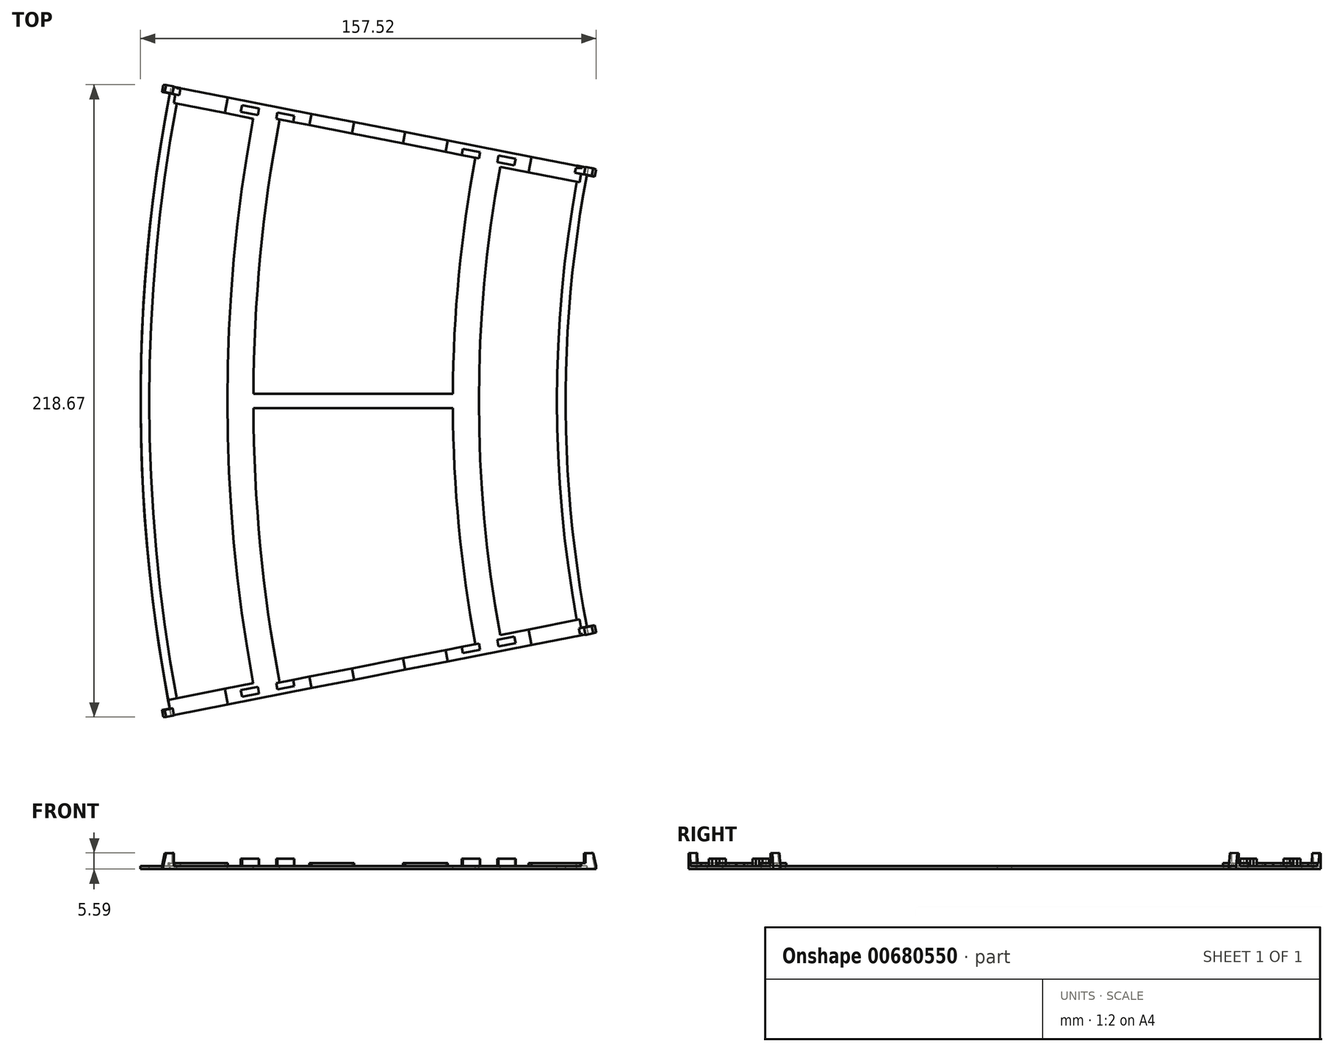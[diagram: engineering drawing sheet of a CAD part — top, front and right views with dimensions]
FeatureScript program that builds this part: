
annotation { "Feature Type Name" : "Feature", "Feature Type Description" : "" }
export const myFeature = defineFeature(function(context is Context, id is Id, definition is map)
    precondition{}
    {
        {
            var Q0;
            Q0=qCreatedBy(makeId("Front.planeOp"),FACE);
            var sketch = newSketch(context, id + "F0", { "sketchPlane" : qUnion([Q0])});
            skLineSegment(sketch, "E0", {"start": v(0, 1.91) * mm, "end": v(570.67, 0) * mm});
            skLineSegment(sketch, "E1", {"start": v(570.67, 0) * mm, "end": v(553.13, -97.53) * mm});
            skLineSegment(sketch, "E2", {"start": v(553.13, -97.53) * mm, "end": v(0, 1.91) * mm});
            skLineSegment(sketch, "E3", {"start": v(0, 1.91) * mm, "end": v(0.03, 10.91) * mm});
            skLineSegment(sketch, "E4", {"start": v(0.03, 10.91) * mm, "end": v(156.03, 10.39) * mm});
            skLineSegment(sketch, "E5", {"start": v(156.03, 10.39) * mm, "end": v(156, 1.39) * mm});
            skLineSegment(sketch, "E6", {"start": v(156, 1.39) * mm, "end": v(155.97, -7.61) * mm});
            skLineSegment(sketch, "E7", {"start": v(155.97, -7.61) * mm, "end": v(-0.03, -7.09) * mm});
            skLineSegment(sketch, "E8", {"start": v(-0.03, -7.09) * mm, "end": v(0, 1.91) * mm});
            skLineSegment(sketch, "E9", {"start": v(4.53, 10.9) * mm, "end": v(4.47, -7.1) * mm});
            skLineSegment(sketch, "E10", {"start": v(151.53, 10.4) * mm, "end": v(151.47, -7.6) * mm});
            skSolve(sketch);
        }
        {
            var Q0;
            {var subQ0=sQuery(id+"F0.wireOp",EDGE,"E9");var subQ1=sQuery(id+"F0.wireOp",EDGE,"E0");var subQ2=makeQuery(id+"F0.imprint","INTERSECT",VERTEX,{"derivedFrom":[subQ1,subQ0]});Q0=makeQuery(id+"F0.imprint","IMPRINT",FACE,{"disambiguationData":[TD([[makeQuery(id+"F0.imprint","IMPRINT",EDGE,{"disambiguationData":[TD([[subQ2,-1.0]])],"derivedFrom":subQ1}),1.0]])]});}
            var Q1;
            {var subQ0=sQuery(id+"F0.wireOp",EDGE,"E9");var subQ1=sQuery(id+"F0.wireOp",EDGE,"E0");var subQ2=makeQuery(id+"F0.imprint","INTERSECT",VERTEX,{"derivedFrom":[subQ1,subQ0]});Q1=makeQuery(id+"F0.imprint","IMPRINT",FACE,{"disambiguationData":[TD([[makeQuery(id+"F0.imprint","IMPRINT",EDGE,{"disambiguationData":[TD([[subQ2,-1.0]])],"derivedFrom":subQ1}),-1.0]])]});}
            var Q2;
            {var subQ0=sQuery(id+"F0.wireOp",EDGE,"E7");var subQ1=sQuery(id+"F0.wireOp",EDGE,"E2");var subQ2=makeQuery(id+"F0.imprint","INTERSECT",VERTEX,{"derivedFrom":[subQ1,subQ0]});Q2=makeQuery(id+"F0.imprint","IMPRINT",FACE,{"disambiguationData":[TD([[makeQuery(id+"F0.imprint","IMPRINT",EDGE,{"disambiguationData":[TD([[subQ2,-1.0]])],"derivedFrom":subQ1}),1.0]])]});}
            var Q3;
            Q3=sQuery(id+"F0.wireOp",EDGE,"E1");
            revolve(context, id + "F1", {"entities" : qUnion([Q0, Q1, Q2]), "axis" : qUnion([Q3]), "revolveType" : RevolveType.SYMMETRIC, "angle" : 22.5 * degree});
        }
        {
            var Q0;
            Q0=qCreatedBy(makeId("Front.planeOp"),FACE);
            var sketch = newSketch(context, id + "F2", { "sketchPlane" : qUnion([Q0])});
            skLineSegment(sketch, "E11.bottom", {"start": v(-4.32, 0) * mm, "end": v(170.27, 0) * mm});
            skLineSegment(sketch, "E11.top", {"start": v(-4.32, -12.77) * mm, "end": v(170.27, -12.77) * mm});
            skLineSegment(sketch, "E11.left", {"start": v(-4.32, 0) * mm, "end": v(-4.32, -12.77) * mm});
            skLineSegment(sketch, "E11.right", {"start": v(170.27, 0) * mm, "end": v(170.27, -12.77) * mm});
            skLineSegment(sketch, "E12.bottom", {"start": v(-4.39, 1) * mm, "end": v(170.27, 1) * mm});
            skLineSegment(sketch, "E12.top", {"start": v(-4.39, 14.98) * mm, "end": v(170.27, 14.98) * mm});
            skLineSegment(sketch, "E12.left", {"start": v(-4.39, 1) * mm, "end": v(-4.39, 14.98) * mm});
            skLineSegment(sketch, "E12.right", {"start": v(170.27, 1) * mm, "end": v(170.27, 14.98) * mm});
            skSolve(sketch);
        }
        {
            var Q0;
            Q0=makeQuery(id+"F2.imprint","IMPRINT",FACE,{"disambiguationData":[TD([[makeQuery(id+"F2.imprint","IMPRINT",EDGE,{"derivedFrom":sQuery(id+"F2.wireOp",EDGE,"E12.bottom")}),1.0]])]});
            var Q1;
            Q1=makeQuery(id+"F2.imprint","IMPRINT",FACE,{"disambiguationData":[TD([[makeQuery(id+"F2.imprint","IMPRINT",EDGE,{"derivedFrom":sQuery(id+"F2.wireOp",EDGE,"E11.bottom")}),-1.0]])]});
            extrude(context, id + "F3", {"entities" : qUnion([Q0, Q1]), "operationType" : NewBodyOperationType.REMOVE, "endBound" : BoundingType.SYMMETRIC, "depth" : 250 * mm, "offsetDistance" : 25 * mm});
        }
        {
            var Q0;
            Q0=makeQuery(id+"F3.boolean.opBoolean","COPY",FACE,{"derivedFrom":makeQuery(id+"F3.opExtrude","SWEPT_FACE",FACE,{"disambiguationData":[OSD([sQuery(id+"F2.wireOp",EDGE,"E12.bottom")])]})});
            var sketch = newSketch(context, id + "F4", { "sketchPlane" : qUnion([Q0])});
            skArc(sketch, "E13", {"start": v(16.97, 102.83) * mm, "mid": v(7.5, 0) * mm, "end": v(16.97, -102.83) * mm});
            skArc(sketch, "E14", {"start": v(43.47, 97.64) * mm, "mid": v(34.5, 0) * mm, "end": v(43.47, -97.64) * mm});
            skArc(sketch, "E15", {"start": v(52.57, 97.39) * mm, "mid": v(45.9, 50.15) * mm, "end": v(43.5, 2.5) * mm});
            skArc(sketch, "E16", {"start": v(120.29, 84.13) * mm, "mid": v(114.57, 43.5) * mm, "end": v(112.5, 2.5) * mm});
            skArc(sketch, "E17", {"start": v(128.85, 80.93) * mm, "mid": v(121.5, 0) * mm, "end": v(128.85, -80.93) * mm});
            skArc(sketch, "E18", {"start": v(155.35, 75.74) * mm, "mid": v(148.5, 0) * mm, "end": v(155.35, -75.74) * mm});
            skLineSegment(sketch, "E19", {"start": v(43.5, 2.5) * mm, "end": v(112.5, 2.5) * mm});
            skLineSegment(sketch, "E20", {"start": v(43.5, -2.5) * mm, "end": v(112.5, -2.5) * mm});
            skArc(sketch, "E21.trimOffspring", {"start": v(43.5, -2.5) * mm, "mid": v(45.9, -50.15) * mm, "end": v(52.57, -97.39) * mm});
            skArc(sketch, "E22.trimOffspring", {"start": v(112.5, -2.5) * mm, "mid": v(114.57, -43.5) * mm, "end": v(120.29, -84.13) * mm});
            skLineSegment(sketch, "E23", {"start": v(16.97, 102.83) * mm, "end": v(43.47, 97.64) * mm});
            skLineSegment(sketch, "E24", {"start": v(52.57, 97.39) * mm, "end": v(120.29, 84.13) * mm});
            skLineSegment(sketch, "E25", {"start": v(128.85, 80.93) * mm, "end": v(155.35, 75.74) * mm});
            skLineSegment(sketch, "E26", {"start": v(16.97, -102.83) * mm, "end": v(43.47, -97.64) * mm});
            skLineSegment(sketch, "E27", {"start": v(52.57, -97.39) * mm, "end": v(120.29, -84.13) * mm});
            skLineSegment(sketch, "E28", {"start": v(128.85, -80.93) * mm, "end": v(155.35, -75.74) * mm});
            skSolve(sketch);
        }
        {
            var Q0;
            Q0=makeQuery(id+"F4.imprint","IMPRINT",FACE,{"disambiguationData":[TD([[makeQuery(id+"F4.imprint","IMPRINT",EDGE,{"derivedFrom":sQuery(id+"F4.wireOp",EDGE,"E13")}),1.0]])]});
            var Q1;
            Q1=makeQuery(id+"F4.imprint","IMPRINT",FACE,{"disambiguationData":[TD([[makeQuery(id+"F4.imprint","IMPRINT",EDGE,{"derivedFrom":sQuery(id+"F4.wireOp",EDGE,"E15")}),1.0]])]});
            var Q2;
            Q2=makeQuery(id+"F4.imprint","IMPRINT",FACE,{"disambiguationData":[TD([[makeQuery(id+"F4.imprint","IMPRINT",EDGE,{"derivedFrom":sQuery(id+"F4.wireOp",EDGE,"E20")}),-1.0]])]});
            var Q3;
            Q3=makeQuery(id+"F4.imprint","IMPRINT",FACE,{"disambiguationData":[TD([[makeQuery(id+"F4.imprint","IMPRINT",EDGE,{"derivedFrom":sQuery(id+"F4.wireOp",EDGE,"E17")}),1.0]])]});
            extrude(context, id + "F5", {"entities" : qUnion([Q0, Q1, Q2, Q3]), "operationType" : NewBodyOperationType.REMOVE, "endBound" : BoundingType.THROUGH_ALL, "oppositeDirection" : true, "depth" : 25 * mm, "offsetDistance" : 25 * mm});
        }
        {
            var Q0;
            Q0=makeQuery(id+"F3.boolean.opBoolean","COPY",FACE,{"derivedFrom":makeQuery(id+"F3.opExtrude","SWEPT_FACE",FACE,{"disambiguationData":[OSD([sQuery(id+"F2.wireOp",EDGE,"E12.bottom")])]})});
            var sketch = newSketch(context, id + "F6", { "sketchPlane" : qUnion([Q0])});
            skLineSegment(sketch, "E29", {"start": v(115.58, 85.05) * mm, "end": v(121.47, 83.9) * mm});
            skLineSegment(sketch, "E30", {"start": v(121.47, 83.9) * mm, "end": v(121.9, 86.06) * mm});
            skLineSegment(sketch, "E31", {"start": v(121.9, 86.06) * mm, "end": v(116, 87.21) * mm});
            skLineSegment(sketch, "E32", {"start": v(116, 87.21) * mm, "end": v(115.58, 85.05) * mm});
            skLineSegment(sketch, "E33", {"start": v(127.85, 82.65) * mm, "end": v(133.73, 81.5) * mm});
            skLineSegment(sketch, "E34", {"start": v(133.73, 81.5) * mm, "end": v(134.18, 83.76) * mm});
            skLineSegment(sketch, "E35", {"start": v(134.18, 83.76) * mm, "end": v(128.29, 84.9) * mm});
            skLineSegment(sketch, "E36", {"start": v(128.29, 84.9) * mm, "end": v(127.85, 82.65) * mm});
            skLineSegment(sketch, "E37", {"start": v(115.58, -85.05) * mm, "end": v(121.47, -83.9) * mm});
            skLineSegment(sketch, "E38", {"start": v(121.47, -83.9) * mm, "end": v(121.9, -86.06) * mm});
            skLineSegment(sketch, "E39", {"start": v(121.9, -86.06) * mm, "end": v(116, -87.21) * mm});
            skLineSegment(sketch, "E40", {"start": v(116, -87.21) * mm, "end": v(115.58, -85.05) * mm});
            skLineSegment(sketch, "E41", {"start": v(127.85, -82.65) * mm, "end": v(133.73, -81.5) * mm});
            skLineSegment(sketch, "E42", {"start": v(133.73, -81.5) * mm, "end": v(134.18, -83.76) * mm});
            skLineSegment(sketch, "E43", {"start": v(134.18, -83.76) * mm, "end": v(128.29, -84.9) * mm});
            skLineSegment(sketch, "E44", {"start": v(128.29, -84.9) * mm, "end": v(127.85, -82.65) * mm});
            skLineSegment(sketch, "E45", {"start": v(57.28, 96.47) * mm, "end": v(51.4, 97.62) * mm});
            skLineSegment(sketch, "E46", {"start": v(51.4, 97.62) * mm, "end": v(51.82, 99.78) * mm});
            skLineSegment(sketch, "E47", {"start": v(51.82, 99.78) * mm, "end": v(57.7, 98.63) * mm});
            skLineSegment(sketch, "E48", {"start": v(57.7, 98.63) * mm, "end": v(57.28, 96.47) * mm});
            skLineSegment(sketch, "E49", {"start": v(45.46, 101.12) * mm, "end": v(39.57, 102.28) * mm});
            skLineSegment(sketch, "E50", {"start": v(39.57, 102.28) * mm, "end": v(39.13, 100.02) * mm});
            skLineSegment(sketch, "E51", {"start": v(39.13, 100.02) * mm, "end": v(45.02, 98.87) * mm});
            skLineSegment(sketch, "E52", {"start": v(45.02, 98.87) * mm, "end": v(45.46, 101.12) * mm});
            skLineSegment(sketch, "E53", {"start": v(57.28, -96.47) * mm, "end": v(51.4, -97.62) * mm});
            skLineSegment(sketch, "E54", {"start": v(51.4, -97.62) * mm, "end": v(51.82, -99.78) * mm});
            skLineSegment(sketch, "E55", {"start": v(51.82, -99.78) * mm, "end": v(57.7, -98.63) * mm});
            skLineSegment(sketch, "E56", {"start": v(57.7, -98.63) * mm, "end": v(57.28, -96.47) * mm});
            skLineSegment(sketch, "E57", {"start": v(45.02, -98.87) * mm, "end": v(39.13, -100.02) * mm});
            skLineSegment(sketch, "E58", {"start": v(39.13, -100.02) * mm, "end": v(39.57, -102.28) * mm});
            skLineSegment(sketch, "E59", {"start": v(39.57, -102.28) * mm, "end": v(45.46, -101.12) * mm});
            skLineSegment(sketch, "E60", {"start": v(45.46, -101.12) * mm, "end": v(45.02, -98.87) * mm});
            skSolve(sketch);
        }
        {
            var Q0;
            Q0=makeQuery(id+"F6.imprint","IMPRINT",FACE,{"disambiguationData":[TD([[makeQuery(id+"F6.imprint","IMPRINT",EDGE,{"derivedFrom":sQuery(id+"F6.wireOp",EDGE,"E49")}),1.0]])]});
            var Q1;
            {var subQ0=sQuery(id+"F6.wireOp",EDGE,"E46");Q1=makeQuery(id+"F6.imprint","IMPRINT",FACE,{"disambiguationData":[TD([[makeQuery(id+"F6.imprint","IMPRINT",EDGE,{"derivedFrom":subQ0}),-1.0]])]});}
            var Q2;
            {var subQ0=sQuery(id+"F6.wireOp",EDGE,"E30");Q2=makeQuery(id+"F6.imprint","IMPRINT",FACE,{"disambiguationData":[TD([[makeQuery(id+"F6.imprint","IMPRINT",EDGE,{"derivedFrom":subQ0}),1.0]])]});}
            var Q3;
            Q3=makeQuery(id+"F6.imprint","IMPRINT",FACE,{"disambiguationData":[TD([[makeQuery(id+"F6.imprint","IMPRINT",EDGE,{"derivedFrom":sQuery(id+"F6.wireOp",EDGE,"E33")}),1.0]])]});
            var Q4;
            {var subQ0=sQuery(id+"F6.wireOp",EDGE,"E38");Q4=makeQuery(id+"F6.imprint","IMPRINT",FACE,{"disambiguationData":[TD([[makeQuery(id+"F6.imprint","IMPRINT",EDGE,{"derivedFrom":subQ0}),-1.0]])]});}
            var Q5;
            Q5=makeQuery(id+"F6.imprint","IMPRINT",FACE,{"disambiguationData":[TD([[makeQuery(id+"F6.imprint","IMPRINT",EDGE,{"derivedFrom":sQuery(id+"F6.wireOp",EDGE,"E41")}),-1.0]])]});
            var Q6;
            Q6=makeQuery(id+"F6.imprint","IMPRINT",FACE,{"disambiguationData":[TD([[makeQuery(id+"F6.imprint","IMPRINT",EDGE,{"derivedFrom":sQuery(id+"F6.wireOp",EDGE,"E57")}),1.0]])]});
            var Q7;
            {var subQ0=sQuery(id+"F6.wireOp",EDGE,"E54");Q7=makeQuery(id+"F6.imprint","IMPRINT",FACE,{"disambiguationData":[TD([[makeQuery(id+"F6.imprint","IMPRINT",EDGE,{"derivedFrom":subQ0}),1.0]])]});}
            extrude(context, id + "F7", {"entities" : qUnion([Q0, Q1, Q2, Q3, Q4, Q5, Q6, Q7]), "operationType" : NewBodyOperationType.ADD, "depth" : 2.5 * mm, "offsetDistance" : 25 * mm});
        }
        {
            var Q0;
            Q0=makeQuery(id+"F3.boolean.opBoolean","COPY",FACE,{"derivedFrom":makeQuery(id+"F3.opExtrude","SWEPT_FACE",FACE,{"disambiguationData":[OSD([sQuery(id+"F2.wireOp",EDGE,"E12.bottom")])]})});
            var sketch = newSketch(context, id + "F8", { "sketchPlane" : qUnion([Q0])});
            skLineSegment(sketch, "E61", {"start": v(17.01, 108.43) * mm, "end": v(34.68, 104.97) * mm});
            skLineSegment(sketch, "E62", {"start": v(34.68, 104.97) * mm, "end": v(33.62, 99.57) * mm});
            skLineSegment(sketch, "E63", {"start": v(15.96, 103.03) * mm, "end": v(17.01, 108.43) * mm});
            skLineSegment(sketch, "E64", {"start": v(157.35, 80.95) * mm, "end": v(156.3, 75.55) * mm});
            skLineSegment(sketch, "E65", {"start": v(156.3, 75.55) * mm, "end": v(138.63, 79.01) * mm});
            skLineSegment(sketch, "E66", {"start": v(138.63, 79.01) * mm, "end": v(139.69, 84.4) * mm});
            skLineSegment(sketch, "E67", {"start": v(139.69, 84.4) * mm, "end": v(157.35, 80.95) * mm});
            skLineSegment(sketch, "E68", {"start": v(63.63, 99.3) * mm, "end": v(78.35, 96.42) * mm});
            skLineSegment(sketch, "E69", {"start": v(78.35, 96.42) * mm, "end": v(77.58, 92.5) * mm});
            skLineSegment(sketch, "E70", {"start": v(77.58, 92.5) * mm, "end": v(62.86, 95.37) * mm});
            skLineSegment(sketch, "E71", {"start": v(62.86, 95.37) * mm, "end": v(63.63, 99.3) * mm});
            skLineSegment(sketch, "E72", {"start": v(96.01, 92.96) * mm, "end": v(110.73, 90.08) * mm});
            skLineSegment(sketch, "E73", {"start": v(110.73, 90.08) * mm, "end": v(109.97, 86.15) * mm});
            skLineSegment(sketch, "E74", {"start": v(109.97, 86.15) * mm, "end": v(95.25, 89.03) * mm});
            skLineSegment(sketch, "E75", {"start": v(95.25, 89.03) * mm, "end": v(96.01, 92.96) * mm});
            skLineSegment(sketch, "E76", {"start": v(15.96, 103.03) * mm, "end": v(33.62, 99.57) * mm});
            skLineSegment(sketch, "E77", {"start": v(156.3, -75.55) * mm, "end": v(157.35, -80.95) * mm});
            skLineSegment(sketch, "E78", {"start": v(157.35, -80.95) * mm, "end": v(139.69, -84.4) * mm});
            skLineSegment(sketch, "E79", {"start": v(139.69, -84.4) * mm, "end": v(138.63, -79.01) * mm});
            skLineSegment(sketch, "E80", {"start": v(138.63, -79.01) * mm, "end": v(156.3, -75.55) * mm});
            skLineSegment(sketch, "E81", {"start": v(95.25, -89.03) * mm, "end": v(109.97, -86.15) * mm});
            skLineSegment(sketch, "E82", {"start": v(109.97, -86.15) * mm, "end": v(110.73, -90.08) * mm});
            skLineSegment(sketch, "E83", {"start": v(110.73, -90.08) * mm, "end": v(96.01, -92.96) * mm});
            skLineSegment(sketch, "E84", {"start": v(96.01, -92.96) * mm, "end": v(95.25, -89.03) * mm});
            skLineSegment(sketch, "E85", {"start": v(15.05, -108.81) * mm, "end": v(14.02, -103.4) * mm});
            skLineSegment(sketch, "E86", {"start": v(14.02, -103.4) * mm, "end": v(33.62, -99.57) * mm});
            skLineSegment(sketch, "E87", {"start": v(33.62, -99.57) * mm, "end": v(34.68, -104.97) * mm});
            skLineSegment(sketch, "E88", {"start": v(34.68, -104.97) * mm, "end": v(15.05, -108.81) * mm});
            skLineSegment(sketch, "E89", {"start": v(63.63, -99.3) * mm, "end": v(78.35, -96.42) * mm});
            skLineSegment(sketch, "E90", {"start": v(78.35, -96.42) * mm, "end": v(77.58, -92.5) * mm});
            skLineSegment(sketch, "E91", {"start": v(77.58, -92.5) * mm, "end": v(62.86, -95.37) * mm});
            skLineSegment(sketch, "E92", {"start": v(62.86, -95.37) * mm, "end": v(63.63, -99.3) * mm});
            skSolve(sketch);
        }
        {
            var Q0;
            Q0=makeQuery(id+"F8.imprint","IMPRINT",FACE,{"disambiguationData":[TD([[makeQuery(id+"F8.imprint","IMPRINT",EDGE,{"derivedFrom":sQuery(id+"F8.wireOp",EDGE,"E61")}),1.0]])]});
            var Q1;
            Q1=makeQuery(id+"F8.imprint","IMPRINT",FACE,{"disambiguationData":[TD([[makeQuery(id+"F8.imprint","IMPRINT",EDGE,{"derivedFrom":sQuery(id+"F8.wireOp",EDGE,"E68")}),1.0]])]});
            var Q2;
            Q2=makeQuery(id+"F8.imprint","IMPRINT",FACE,{"disambiguationData":[TD([[makeQuery(id+"F8.imprint","IMPRINT",EDGE,{"derivedFrom":sQuery(id+"F8.wireOp",EDGE,"E72")}),1.0]])]});
            var Q3;
            {var subQ3=sQuery(id+"F8.wireOp",EDGE,"E64");Q3=makeQuery(id+"F8.imprint","IMPRINT",FACE,{"disambiguationData":[TD([[makeQuery(id+"F8.imprint","IMPRINT",EDGE,{"derivedFrom":subQ3}),-1.0]])]});}
            var Q4;
            {var subQ2=sQuery(id+"F8.wireOp",EDGE,"E77");Q4=makeQuery(id+"F8.imprint","IMPRINT",FACE,{"disambiguationData":[TD([[makeQuery(id+"F8.imprint","IMPRINT",EDGE,{"derivedFrom":subQ2}),-1.0]])]});}
            var Q5;
            Q5=makeQuery(id+"F8.imprint","IMPRINT",FACE,{"disambiguationData":[TD([[makeQuery(id+"F8.imprint","IMPRINT",EDGE,{"derivedFrom":sQuery(id+"F8.wireOp",EDGE,"E81")}),-1.0]])]});
            var Q6;
            Q6=makeQuery(id+"F8.imprint","IMPRINT",FACE,{"disambiguationData":[TD([[makeQuery(id+"F8.imprint","IMPRINT",EDGE,{"derivedFrom":sQuery(id+"F8.wireOp",EDGE,"E89")}),-1.0]])]});
            var Q7;
            {var subQ3=sQuery(id+"F8.wireOp",EDGE,"E85");Q7=makeQuery(id+"F8.imprint","IMPRINT",FACE,{"disambiguationData":[TD([[makeQuery(id+"F8.imprint","IMPRINT",EDGE,{"derivedFrom":subQ3}),-1.0]])]});}
            extrude(context, id + "F9", {"entities" : qUnion([Q0, Q1, Q2, Q3, Q4, Q5, Q6, Q7]), "operationType" : NewBodyOperationType.ADD, "depth" : 1 * mm, "offsetDistance" : 25 * mm});
        }
        {
            var Q0;
            Q0=makeQuery(id+"F1.opRevolve","CAP_FACE",FACE,{"disambiguationData":[OSD([sQuery(id+"F0.wireOp",EDGE,"E4"),sQuery(id+"F0.wireOp",EDGE,"E7"),sQuery(id+"F0.wireOp",EDGE,"E9"),sQuery(id+"F0.wireOp",EDGE,"E10")])],"isStart":true});
            var sketch = newSketch(context, id + "F10", { "sketchPlane" : qUnion([Q0])});
            skLineSegment(sketch, "E93", {"start": v(140.89, 2.85) * mm, "end": v(143.64, 2.85) * mm});
            skLineSegment(sketch, "E94", {"start": v(143.64, 2.85) * mm, "end": v(143.64, 3.84) * mm});
            skLineSegment(sketch, "E95", {"start": v(143.64, 3.84) * mm, "end": v(142.64, 8.29) * mm});
            skLineSegment(sketch, "E96", {"start": v(142.64, 8.29) * mm, "end": v(139.89, 8.29) * mm});
            skLineSegment(sketch, "E97", {"start": v(139.89, 8.29) * mm, "end": v(139.89, 4.84) * mm});
            skLineSegment(sketch, "E98", {"start": v(139.89, 4.84) * mm, "end": v(138.06, 4.84) * mm});
            skLineSegment(sketch, "E99", {"start": v(138.9, 2.85) * mm, "end": v(140.89, 2.85) * mm});
            skLineSegment(sketch, "E100", {"start": v(138.9, 2.85) * mm, "end": v(138.06, 4.84) * mm});
            skLineSegment(sketch, "E101", {"start": v(-6.1, 5.83) * mm, "end": v(-5.1, 5.83) * mm});
            skLineSegment(sketch, "E102", {"start": v(-5.1, 5.83) * mm, "end": v(-5.1, 9.28) * mm});
            skLineSegment(sketch, "E103", {"start": v(-5.1, 9.28) * mm, "end": v(-7.85, 9.28) * mm});
            skLineSegment(sketch, "E104", {"start": v(-7.85, 9.28) * mm, "end": v(-8.85, 4.78) * mm});
            skLineSegment(sketch, "E105", {"start": v(-8.85, 4.78) * mm, "end": v(-8.85, 3.85) * mm});
            skLineSegment(sketch, "E106", {"start": v(-8.85, 3.85) * mm, "end": v(-5.1, 3.85) * mm});
            skLineSegment(sketch, "E107", {"start": v(-5.1, 3.85) * mm, "end": v(-5.1, 5.83) * mm});
            skSolve(sketch);
        }
        {
            var Q0;
            {var subQ7=sQuery(id+"F10.wireOp",EDGE,"E102");Q0=makeQuery(id+"F10.imprint","IMPRINT",FACE,{"disambiguationData":[TD([[makeQuery(id+"F10.imprint","IMPRINT",EDGE,{"derivedFrom":subQ7}),1.0]])]});}
            var Q1;
            {var subQ0=sQuery(id+"F10.wireOp",EDGE,"E107");var subQ1=sQuery(id+"F10.wireOp",EDGE,"E106");var subQ2=makeQuery(id+"F10.imprint","INTERSECT",VERTEX,{"derivedFrom":[subQ1,subQ0]});Q1=makeQuery(id+"F10.imprint","IMPRINT",FACE,{"disambiguationData":[TD([[makeQuery(id+"F10.imprint","IMPRINT",EDGE,{"disambiguationData":[TD([[subQ2,1.0]])],"derivedFrom":subQ1}),1.0]])]});}
            var Q2;
            {var subQ0=sQuery(id+"F10.wireOp",EDGE,"E93");Q2=makeQuery(id+"F10.imprint","IMPRINT",FACE,{"disambiguationData":[TD([[makeQuery(id+"F10.imprint","IMPRINT",EDGE,{"derivedFrom":subQ0}),1.0]])]});}
            var Q3;
            {var subQ9=sQuery(id+"F10.wireOp",EDGE,"E99");Q3=makeQuery(id+"F10.imprint","IMPRINT",FACE,{"disambiguationData":[TD([[makeQuery(id+"F10.imprint","IMPRINT",EDGE,{"derivedFrom":subQ9}),1.0]])]});}
            extrude(context, id + "F11", {"entities" : qUnion([Q0, Q1, Q2, Q3]), "operationType" : NewBodyOperationType.ADD, "oppositeDirection" : true, "depth" : 2.5 * mm, "offsetDistance" : 25 * mm});
        }
        {
            var Q0;
            Q0=makeQuery(id+"F1.opRevolve","CAP_FACE",FACE,{"disambiguationData":[OSD([sQuery(id+"F0.wireOp",EDGE,"E4"),sQuery(id+"F0.wireOp",EDGE,"E7"),sQuery(id+"F0.wireOp",EDGE,"E9"),sQuery(id+"F0.wireOp",EDGE,"E10")])],"isStart":false});
            var sketch = newSketch(context, id + "F12", { "sketchPlane" : qUnion([Q0])});
            skLineSegment(sketch, "E108", {"start": v(-136.97, 2.83) * mm, "end": v(-143.64, 2.83) * mm});
            skLineSegment(sketch, "E109", {"start": v(-143.64, 2.83) * mm, "end": v(-143.64, 3.78) * mm});
            skLineSegment(sketch, "E110", {"start": v(-143.64, 3.78) * mm, "end": v(-142.64, 8.28) * mm});
            skLineSegment(sketch, "E111", {"start": v(-142.64, 8.28) * mm, "end": v(-139.9, 8.28) * mm});
            skLineSegment(sketch, "E112", {"start": v(-139.9, 8.28) * mm, "end": v(-139.9, 4.83) * mm});
            skLineSegment(sketch, "E113", {"start": v(-139.9, 4.83) * mm, "end": v(-136.72, 4.83) * mm});
            skLineSegment(sketch, "E114", {"start": v(-136.72, 4.83) * mm, "end": v(-136.97, 2.83) * mm});
            skLineSegment(sketch, "E115", {"start": v(6.1, 3.8) * mm, "end": v(8.85, 3.8) * mm});
            skLineSegment(sketch, "E116", {"start": v(8.85, 3.8) * mm, "end": v(8.85, 4.75) * mm});
            skLineSegment(sketch, "E117", {"start": v(8.85, 4.75) * mm, "end": v(7.85, 9.25) * mm});
            skLineSegment(sketch, "E118", {"start": v(7.85, 9.25) * mm, "end": v(5.1, 9.25) * mm});
            skLineSegment(sketch, "E119", {"start": v(4.82, 3.8) * mm, "end": v(6.1, 3.8) * mm});
            skLineSegment(sketch, "E120", {"start": v(4.82, 3.8) * mm, "end": v(2.76, 3.8) * mm});
            skLineSegment(sketch, "E121", {"start": v(2.76, 3.8) * mm, "end": v(2.76, 5.8) * mm});
            skLineSegment(sketch, "E122", {"start": v(2.76, 5.8) * mm, "end": v(5.1, 5.8) * mm});
            skLineSegment(sketch, "E123", {"start": v(5.1, 5.8) * mm, "end": v(5.1, 9.25) * mm});
            skSolve(sketch);
        }
        {
            var Q0;
            Q0=makeQuery(id+"F12.imprint","IMPRINT",FACE,{"disambiguationData":[TD([[makeQuery(id+"F12.imprint","IMPRINT",EDGE,{"derivedFrom":sQuery(id+"F12.wireOp",EDGE,"E115")}),1.0]])]});
            var Q1;
            {var subQ0=sQuery(id+"F0.wireOp",EDGE,"E9");var subQ3=makeQuery(id+"F1.opRevolve","CAP_EDGE",EDGE,{"disambiguationData":[OSD([subQ0])],"isStart":false});Q1=makeQuery(id+"F12.imprint","IMPRINT",FACE,{"disambiguationData":[TD([[makeQuery(id+"F12.imprint","IMPRINT",EDGE,{"derivedFrom":subQ3}),-1.0]])]});}
            var Q2;
            {var subQ6=sQuery(id+"F12.wireOp",EDGE,"E109");Q2=makeQuery(id+"F12.imprint","IMPRINT",FACE,{"disambiguationData":[TD([[makeQuery(id+"F12.imprint","IMPRINT",EDGE,{"derivedFrom":subQ6}),-1.0]])]});}
            var Q3;
            {var subQ1=sQuery(id+"F0.wireOp",EDGE,"E10");var subQ7=makeQuery(id+"F1.opRevolve","CAP_EDGE",EDGE,{"disambiguationData":[OSD([subQ1])],"isStart":false});Q3=makeQuery(id+"F12.imprint","IMPRINT",FACE,{"disambiguationData":[TD([[makeQuery(id+"F12.imprint","IMPRINT",EDGE,{"derivedFrom":subQ7}),1.0]])]});}
            extrude(context, id + "F13", {"entities" : qUnion([Q0, Q1, Q2, Q3]), "operationType" : NewBodyOperationType.ADD, "oppositeDirection" : true, "depth" : 2.5 * mm, "offsetDistance" : 25 * mm});
        }
    });
